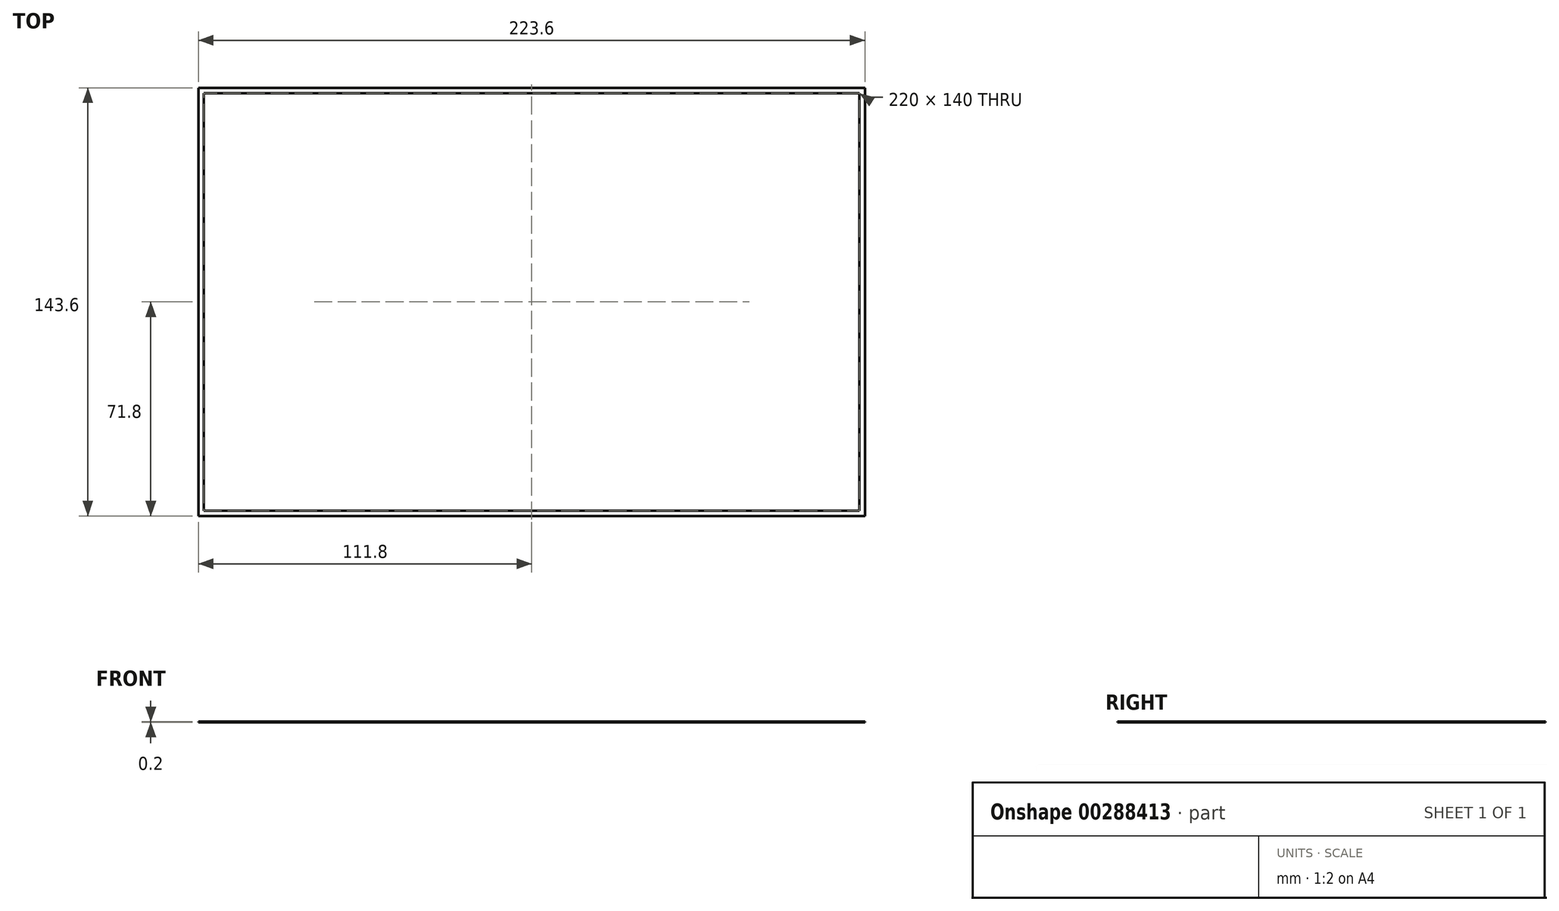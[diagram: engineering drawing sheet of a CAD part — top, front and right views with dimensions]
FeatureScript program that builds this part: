
annotation { "Feature Type Name" : "Feature", "Feature Type Description" : "" }
export const myFeature = defineFeature(function(context is Context, id is Id, definition is map)
    precondition{}
    {
        {
            var Q0;
            Q0=qCreatedBy(makeId("Top.planeOp"),FACE);
            var sketch = newSketch(context, id + "F0", { "sketchPlane" : qUnion([Q0])});
            skLineSegment(sketch, "E0.bottom", {"start": v(-110, 70) * mm, "end": v(110, 70) * mm});
            skLineSegment(sketch, "E0.top", {"start": v(-110, -70) * mm, "end": v(110, -70) * mm});
            skLineSegment(sketch, "E0.left", {"start": v(-110, 70) * mm, "end": v(-110, -70) * mm});
            skLineSegment(sketch, "E0.right", {"start": v(110, 70) * mm, "end": v(110, -70) * mm});
            skPoint(sketch, "E0.middle", {"position": v(0, 0) * mm});
            skLineSegment(sketch, "E1.0", {"start": v(111.8, 71.8) * mm, "end": v(111.8, -71.8) * mm});
            skLineSegment(sketch, "E1.1", {"start": v(-111.8, 71.8) * mm, "end": v(111.8, 71.8) * mm});
            skLineSegment(sketch, "E1.2", {"start": v(-111.8, 71.8) * mm, "end": v(-111.8, -71.8) * mm});
            skLineSegment(sketch, "E1.3", {"start": v(-111.8, -71.8) * mm, "end": v(111.8, -71.8) * mm});
            skSolve(sketch);
        }
        {
            var Q0;
            Q0 = qSketchRegion(id + "F0", true);
            extrude(context, id + "F1", {"entities" : qUnion([Q0]), "depth" : 0.2 * mm});
        }
    });
